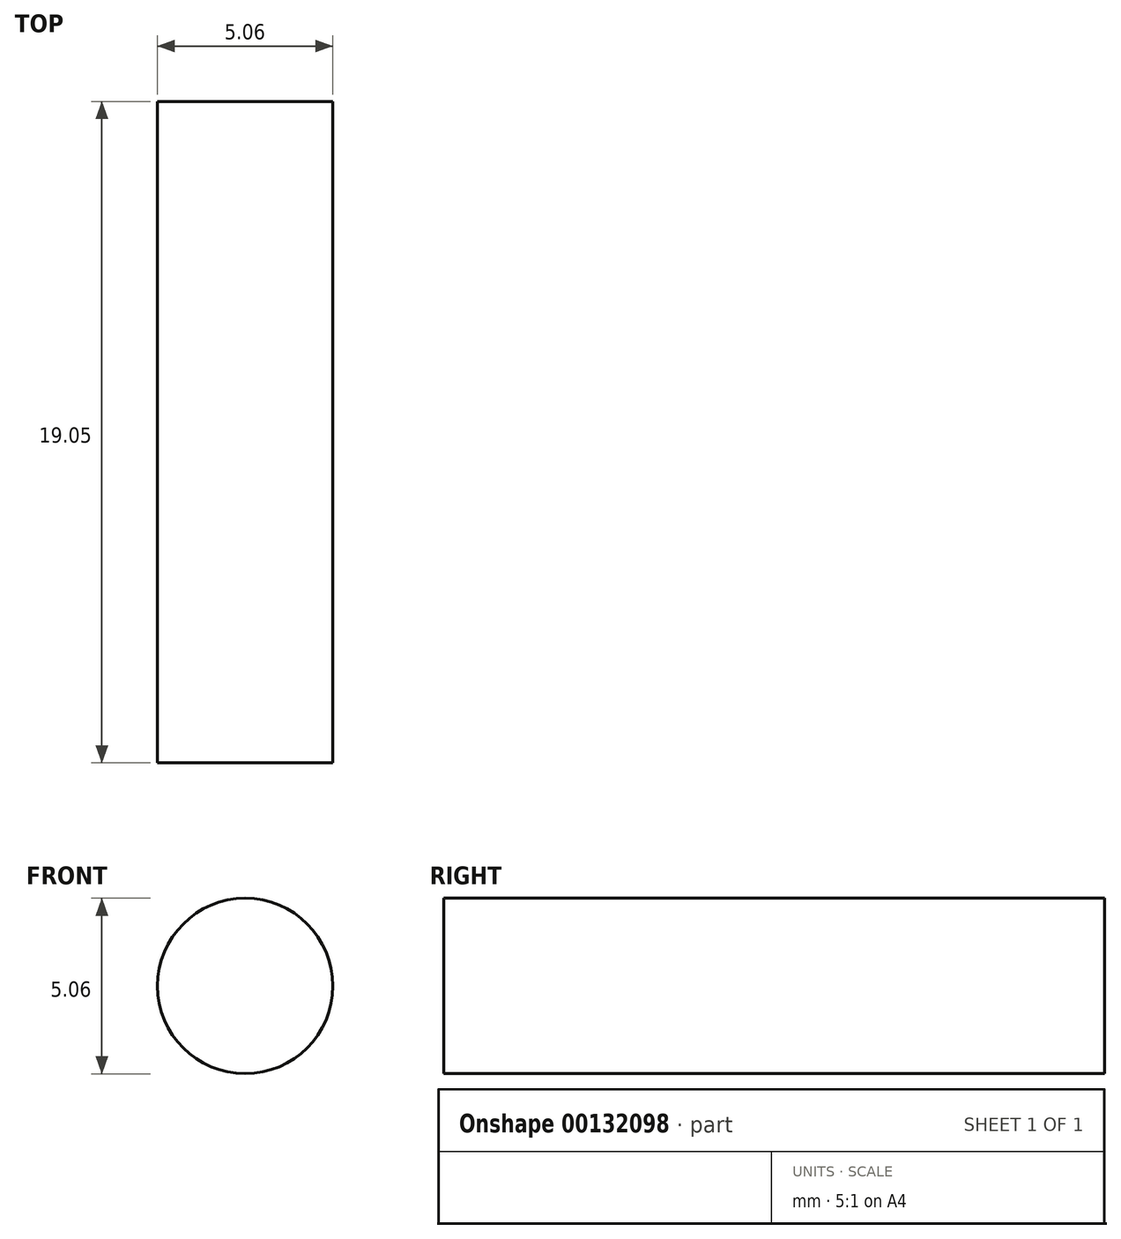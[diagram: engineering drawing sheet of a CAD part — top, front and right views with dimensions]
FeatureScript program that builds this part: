
annotation { "Feature Type Name" : "Feature", "Feature Type Description" : "" }
export const myFeature = defineFeature(function(context is Context, id is Id, definition is map)
    precondition{}
    {
        {
            var Q0;
            Q0=qCreatedBy(makeId("Front.planeOp"),FACE);
            var sketch = newSketch(context, id + "F0", { "sketchPlane" : qUnion([Q0])});
            skCircle(sketch, "E0", {"center": v(0, 0) * mm, "radius": 2.53 * mm});
            skSolve(sketch);
        }
        {
            var Q0;
            Q0 = qSketchRegion(id + "F0", true);
            extrude(context, id + "F1", {"entities" : qUnion([Q0]), "depth" : 19.05 * mm});
        }
    });
